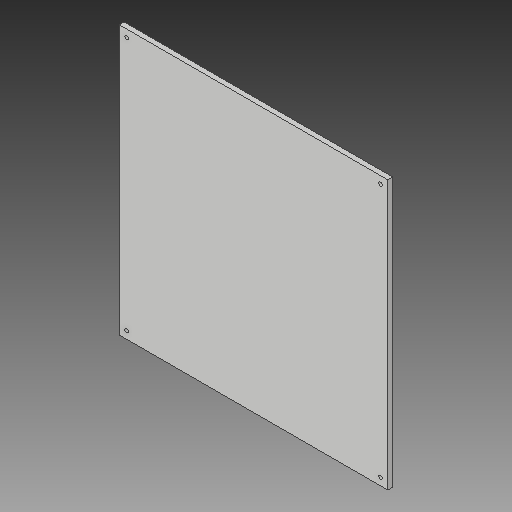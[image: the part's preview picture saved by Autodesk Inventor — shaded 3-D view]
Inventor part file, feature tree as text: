
AUTODESK INVENTOR PART (.ipt)
format: ipt  version: 2018 (Build 220112000, 112)  size: 96,256 bytes
history: native  units: in
note: dims shown in document units (in); Inventor stores cm internally (conversion verified against a paired STEP export)
features: extrude x2, sketch x2, projected_geometry x1
ambient origin geometry x8: Origin, YZ Plane, XZ Plane, XY Plane, X Axis, Y Axis, Z Axis, Center Point
bodies: Solid1 (feature_tree)
feature tree (5):
  extrude  "Extrusion1"  Depth=8.6614in
  extrude  "Extrusion2"  Depth=0.1575in
  sketch  "Sketch1"  dims[d0=8.6614in d1=8.6614in]
  sketch  "Sketch2"  dims[d2=0.1575in d3=0.0in d4=0.2362in d5=0.2362in d6=0.1181in d7=1.5748in d9=360.0deg d11=0.1575in d12=0.0in]
  projected_geometry  "Projected Loop1"
